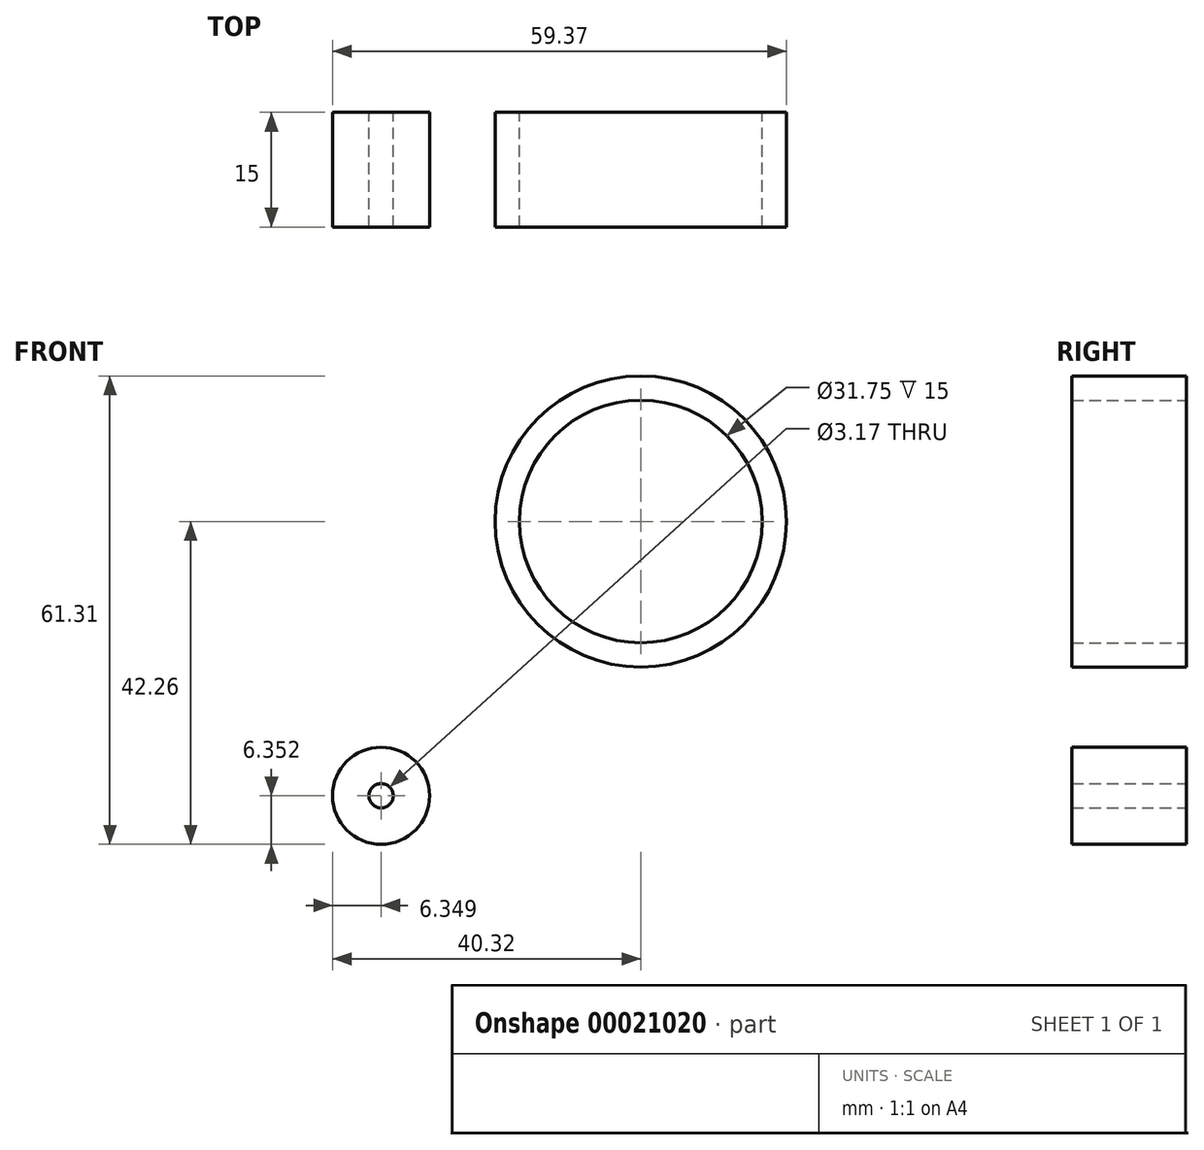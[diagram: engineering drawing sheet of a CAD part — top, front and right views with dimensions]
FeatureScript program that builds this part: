
annotation { "Feature Type Name" : "Feature", "Feature Type Description" : "" }
export const myFeature = defineFeature(function(context is Context, id is Id, definition is map)
    precondition{}
    {
        {
            var Q0;
            Q0=qCreatedBy(makeId("Front.planeOp"),FACE);
            var sketch = newSketch(context, id + "F0", { "sketchPlane" : qUnion([Q0])});
            skCircle(sketch, "E0", {"center": v(0, 0) * mm, "radius": 3.18 * mm});
            skCircle(sketch, "E1", {"center": v(0, 0) * mm, "radius": 0.52 * mm});
            skCircle(sketch, "E2", {"center": v(0, 0) * mm, "radius": 3.17 * mm});
            skCircle(sketch, "E3", {"center": v(0, 0) * mm, "radius": 19.05 * mm});
            skCircle(sketch, "E4", {"center": v(0, 0) * mm, "radius": 15.88 * mm});
            skCircle(sketch, "E5", {"center": v(-33.97, -35.9) * mm, "radius": 6.35 * mm});
            skCircle(sketch, "E6", {"center": v(-33.97, -35.9) * mm, "radius": 1.59 * mm});
            skCircle(sketch, "E7", {"center": v(0, 3.17) * mm, "radius": 1.59 * mm});
            skCircle(sketch, "E8", {"center": v(0, 0) * mm, "radius": 0.8 * mm});
            skCircle(sketch, "E9", {"center": v(0, 0) * mm, "radius": 3.97 * mm});
            skSolve(sketch);
        }
        {
            var Q0;
            Q0 = qSketchRegion(id + "F0", true);
            extrude(context, id + "F1", {"entities" : qUnion([Q0]), "depth" : 6.35 * mm});
        }
        {
            var Q0;
            Q0 = qSketchRegion(id + "F0", true);
            extrude(context, id + "F2", {"entities" : qUnion([Q0]), "operationType" : NewBodyOperationType.ADD, "depth" : 3.17 * mm});
        }
        {
            var Q0;
            Q0=sQuery(id+"F0.wireOp",EDGE,"E0");
            extrude(context, id + "F3", {"bodyType" : ToolBodyType.SURFACE, "surfaceEntities" : qUnion([Q0]), "depth" : 1.59 * mm});
        }
        {
            var Q0;
            Q0 = qSketchRegion(id + "F0", true);
            extrude(context, id + "F4", {"entities" : qUnion([Q0]), "operationType" : NewBodyOperationType.ADD, "depth" : 15 * mm});
        }
    });
